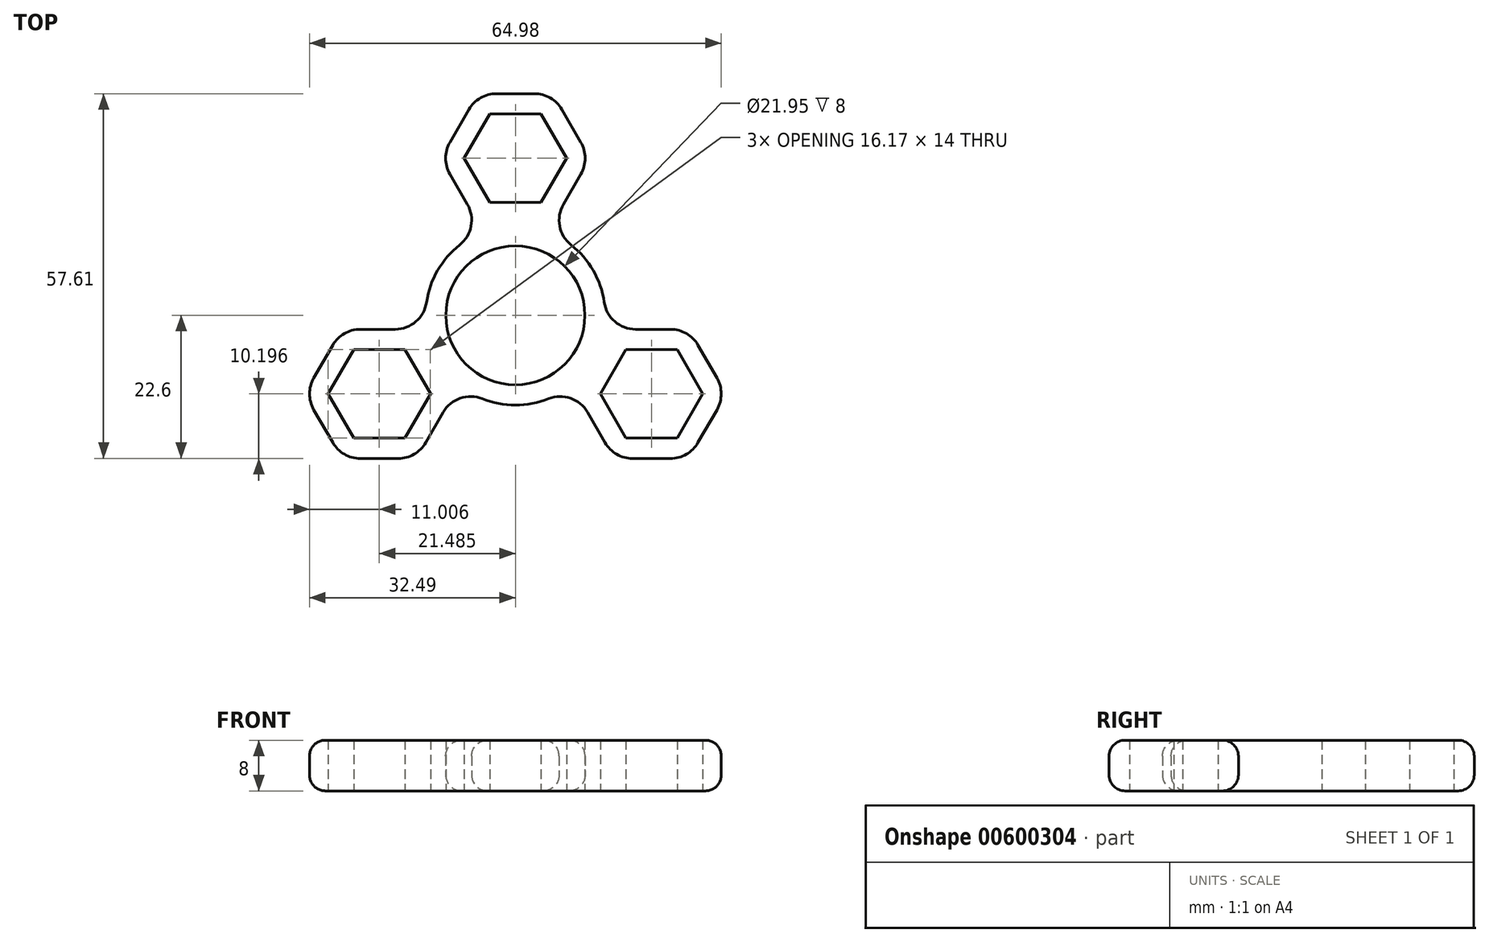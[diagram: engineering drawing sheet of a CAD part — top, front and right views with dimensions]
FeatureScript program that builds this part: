
annotation { "Feature Type Name" : "Feature", "Feature Type Description" : "" }
export const myFeature = defineFeature(function(context is Context, id is Id, definition is map)
    precondition{}
    {
        {
            var Q0;
            Q0=qCreatedBy(makeId("Top.planeOp"),FACE);
            var sketch = newSketch(context, id + "F0", { "sketchPlane" : qUnion([Q0])});
            skCircle(sketch, "E0", {"center": v(0, 0) * mm, "radius": 35.5 * mm, "construction": true});
            skLineSegment(sketch, "E1", {"start": v(0, 24.8) * mm, "end": v(0, 0) * mm, "construction": true});
            skLineSegment(sketch, "E2", {"start": v(0, 0) * mm, "end": v(-21.48, -12.4) * mm, "construction": true});
            skLineSegment(sketch, "E3", {"start": v(0, 0) * mm, "end": v(21.48, -12.4) * mm, "construction": true});
            skCircle(sketch, "E4.cCircle", {"center": v(0, 24.8) * mm, "radius": 7 * mm, "construction": true});
            skLineSegment(sketch, "E4.0", {"start": v(8.08, 24.8) * mm, "end": v(4.04, 17.8) * mm});
            skLineSegment(sketch, "E4.1", {"start": v(4.04, 17.8) * mm, "end": v(-4.04, 17.8) * mm});
            skLineSegment(sketch, "E4.2", {"start": v(-4.04, 17.8) * mm, "end": v(-8.08, 24.8) * mm});
            skLineSegment(sketch, "E4.3", {"start": v(-8.08, 24.8) * mm, "end": v(-4.04, 31.8) * mm});
            skLineSegment(sketch, "E4.4", {"start": v(-4.04, 31.8) * mm, "end": v(4.04, 31.8) * mm});
            skLineSegment(sketch, "E4.5", {"start": v(4.04, 31.8) * mm, "end": v(8.08, 24.8) * mm});
            skPoint(sketch, "E4.0.midPoint", {"position": v(6.06, 21.3) * mm});
            skCircle(sketch, "E5.cCircle", {"center": v(0, 24.8) * mm, "radius": 10.2 * mm, "construction": true});
            skLineSegment(sketch, "E5.0", {"start": v(11.78, 24.8) * mm, "end": v(5.89, 14.6) * mm});
            skLineSegment(sketch, "E5.1", {"start": v(5.89, 14.6) * mm, "end": v(-5.89, 14.6) * mm});
            skLineSegment(sketch, "E5.2", {"start": v(-5.89, 14.6) * mm, "end": v(-11.78, 24.8) * mm});
            skLineSegment(sketch, "E5.3", {"start": v(-11.78, 24.8) * mm, "end": v(-5.89, 35) * mm});
            skLineSegment(sketch, "E5.4", {"start": v(-5.89, 35) * mm, "end": v(5.89, 35) * mm});
            skLineSegment(sketch, "E5.5", {"start": v(5.89, 35) * mm, "end": v(11.78, 24.8) * mm});
            skPoint(sketch, "E5.0.midPoint", {"position": v(8.83, 19.7) * mm});
            skLineSegment(sketch, "E6", {"start": v(-5.89, 14.6) * mm, "end": v(-5.1, 13.23) * mm});
            skLineSegment(sketch, "E7", {"start": v(5.89, 14.6) * mm, "end": v(5.1, 13.23) * mm});
            skCircle(sketch, "E8", {"center": v(0, 0) * mm, "radius": 10.97 * mm});
            skCircle(sketch, "E9.cCircle", {"center": v(21.48, -12.4) * mm, "radius": 7 * mm, "construction": true});
            skLineSegment(sketch, "E9.0", {"start": v(29.57, -12.4) * mm, "end": v(25.53, -19.4) * mm});
            skLineSegment(sketch, "E9.1", {"start": v(25.53, -19.4) * mm, "end": v(17.44, -19.4) * mm});
            skLineSegment(sketch, "E9.2", {"start": v(17.44, -19.4) * mm, "end": v(13.4, -12.4) * mm});
            skLineSegment(sketch, "E9.3", {"start": v(13.4, -12.4) * mm, "end": v(17.44, -5.4) * mm});
            skLineSegment(sketch, "E9.4", {"start": v(17.44, -5.4) * mm, "end": v(25.53, -5.4) * mm});
            skLineSegment(sketch, "E9.5", {"start": v(25.53, -5.4) * mm, "end": v(29.57, -12.4) * mm});
            skPoint(sketch, "E9.0.midPoint", {"position": v(27.55, -15.9) * mm});
            skCircle(sketch, "E10.cCircle", {"center": v(21.48, -12.4) * mm, "radius": 10.2 * mm, "construction": true});
            skLineSegment(sketch, "E10.0", {"start": v(33.26, -12.4) * mm, "end": v(27.37, -22.6) * mm});
            skLineSegment(sketch, "E10.1", {"start": v(27.37, -22.6) * mm, "end": v(15.6, -22.6) * mm});
            skLineSegment(sketch, "E10.2", {"start": v(15.6, -22.6) * mm, "end": v(9.7, -12.4) * mm});
            skLineSegment(sketch, "E10.3", {"start": v(9.7, -12.4) * mm, "end": v(15.6, -2.2) * mm});
            skLineSegment(sketch, "E10.4", {"start": v(15.6, -2.2) * mm, "end": v(27.37, -2.2) * mm});
            skLineSegment(sketch, "E10.5", {"start": v(27.37, -2.2) * mm, "end": v(33.26, -12.4) * mm});
            skPoint(sketch, "E10.0.midPoint", {"position": v(30.32, -17.5) * mm});
            skCircle(sketch, "E11.cCircle", {"center": v(-21.48, -12.4) * mm, "radius": 7 * mm, "construction": true});
            skLineSegment(sketch, "E11.0", {"start": v(-13.4, -12.4) * mm, "end": v(-17.44, -19.4) * mm});
            skLineSegment(sketch, "E11.1", {"start": v(-17.44, -19.4) * mm, "end": v(-25.53, -19.4) * mm});
            skLineSegment(sketch, "E11.2", {"start": v(-25.53, -19.4) * mm, "end": v(-29.57, -12.4) * mm});
            skLineSegment(sketch, "E11.3", {"start": v(-29.57, -12.4) * mm, "end": v(-25.53, -5.4) * mm});
            skLineSegment(sketch, "E11.4", {"start": v(-25.53, -5.4) * mm, "end": v(-17.44, -5.4) * mm});
            skLineSegment(sketch, "E11.5", {"start": v(-17.44, -5.4) * mm, "end": v(-13.4, -12.4) * mm});
            skPoint(sketch, "E11.0.midPoint", {"position": v(-15.42, -15.9) * mm});
            skCircle(sketch, "E12.cCircle", {"center": v(-21.48, -12.4) * mm, "radius": 10.2 * mm, "construction": true});
            skLineSegment(sketch, "E12.0", {"start": v(-9.7, -12.4) * mm, "end": v(-15.6, -22.6) * mm});
            skLineSegment(sketch, "E12.1", {"start": v(-15.6, -22.6) * mm, "end": v(-27.37, -22.6) * mm});
            skLineSegment(sketch, "E12.2", {"start": v(-27.37, -22.6) * mm, "end": v(-33.26, -12.4) * mm});
            skLineSegment(sketch, "E12.3", {"start": v(-33.26, -12.4) * mm, "end": v(-27.37, -2.2) * mm});
            skLineSegment(sketch, "E12.4", {"start": v(-27.37, -2.2) * mm, "end": v(-15.6, -2.2) * mm});
            skLineSegment(sketch, "E12.5", {"start": v(-15.6, -2.2) * mm, "end": v(-9.7, -12.4) * mm});
            skPoint(sketch, "E12.0.midPoint", {"position": v(-12.65, -17.5) * mm});
            skLineSegment(sketch, "E13", {"start": v(-15.6, -2.2) * mm, "end": v(-14, -2.2) * mm});
            skLineSegment(sketch, "E14", {"start": v(-9.7, -12.4) * mm, "end": v(-8.91, -11.02) * mm});
            skLineSegment(sketch, "E15", {"start": v(9.7, -12.4) * mm, "end": v(8.91, -11.02) * mm});
            skLineSegment(sketch, "E16", {"start": v(15.6, -2.2) * mm, "end": v(14, -2.2) * mm});
            skCircle(sketch, "E17", {"center": v(0, 0) * mm, "radius": 14.18 * mm});
            skSolve(sketch);
        }
        {
            var Q0;
            Q0=qSketchRegion(id+"F0",true);
            extrude(context, id + "F1", {"entities" : qUnion([Q0]), "endBound" : BoundingType.SYMMETRIC, "depth" : 8 * mm, "offsetDistance" : 25 * mm});
        }
        {
            var Q0;
            Q0=makeQuery(id+"F1.opExtrude","SWEPT_EDGE",EDGE,{"disambiguationData":[OSD([sQuery(id+"F0.wireOp",EDGE,"O4FCEVp2-a76e-EbQX-IVHh-MGuyo65jWMq8"),sQuery(id+"F0.wireOp",EDGE,"E6")])]});
            var Q1;
            Q1=makeQuery(id+"F1.opExtrude","SWEPT_EDGE",EDGE,{"disambiguationData":[OSD([sQuery(id+"F0.wireOp",EDGE,"O4FCEVp2-a76e-EbQX-IVHh-MGuyo65jWMq8"),sQuery(id+"F0.wireOp",EDGE,"E13")])]});
            var Q2;
            Q2=makeQuery(id+"F1.opExtrude","SWEPT_EDGE",EDGE,{"disambiguationData":[OSD([sQuery(id+"F0.wireOp",EDGE,"O4FCEVp2-a76e-EbQX-IVHh-MGuyo65jWMq8"),sQuery(id+"F0.wireOp",EDGE,"E15")])]});
            var Q3;
            Q3=makeQuery(id+"F1.opExtrude","SWEPT_EDGE",EDGE,{"disambiguationData":[OSD([sQuery(id+"F0.wireOp",EDGE,"O4FCEVp2-a76e-EbQX-IVHh-MGuyo65jWMq8"),sQuery(id+"F0.wireOp",EDGE,"E14")])]});
            var Q4;
            Q4=makeQuery(id+"F1.opExtrude","SWEPT_EDGE",EDGE,{"disambiguationData":[OSD([sQuery(id+"F0.wireOp",EDGE,"O4FCEVp2-a76e-EbQX-IVHh-MGuyo65jWMq8"),sQuery(id+"F0.wireOp",EDGE,"E16")])]});
            var Q5;
            Q5=makeQuery(id+"F1.opExtrude","SWEPT_EDGE",EDGE,{"disambiguationData":[OSD([sQuery(id+"F0.wireOp",EDGE,"O4FCEVp2-a76e-EbQX-IVHh-MGuyo65jWMq8"),sQuery(id+"F0.wireOp",EDGE,"E7")])]});
            var Q6;
            Q6=makeQuery(id+"F1.opExtrude","SWEPT_EDGE",EDGE,{"disambiguationData":[OSD([sQuery(id+"F0.wireOp",EDGE,"E10.4"),sQuery(id+"F0.wireOp",EDGE,"E10.5")])]});
            var Q7;
            Q7=makeQuery(id+"F1.opExtrude","SWEPT_EDGE",EDGE,{"disambiguationData":[OSD([sQuery(id+"F0.wireOp",EDGE,"E10.0"),sQuery(id+"F0.wireOp",EDGE,"E10.5")])]});
            var Q8;
            Q8=makeQuery(id+"F1.opExtrude","SWEPT_EDGE",EDGE,{"disambiguationData":[OSD([sQuery(id+"F0.wireOp",EDGE,"E10.0"),sQuery(id+"F0.wireOp",EDGE,"E10.1")])]});
            var Q9;
            Q9=makeQuery(id+"F1.opExtrude","SWEPT_EDGE",EDGE,{"disambiguationData":[OSD([sQuery(id+"F0.wireOp",EDGE,"E10.1"),sQuery(id+"F0.wireOp",EDGE,"E10.2")])]});
            var Q10;
            Q10=makeQuery(id+"F1.opExtrude","SWEPT_EDGE",EDGE,{"disambiguationData":[OSD([sQuery(id+"F0.wireOp",EDGE,"E12.0"),sQuery(id+"F0.wireOp",EDGE,"E12.1")])]});
            var Q11;
            Q11=makeQuery(id+"F1.opExtrude","SWEPT_EDGE",EDGE,{"disambiguationData":[OSD([sQuery(id+"F0.wireOp",EDGE,"E12.1"),sQuery(id+"F0.wireOp",EDGE,"E12.2")])]});
            var Q12;
            Q12=makeQuery(id+"F1.opExtrude","SWEPT_EDGE",EDGE,{"disambiguationData":[OSD([sQuery(id+"F0.wireOp",EDGE,"E12.2"),sQuery(id+"F0.wireOp",EDGE,"E12.3")])]});
            var Q13;
            Q13=makeQuery(id+"F1.opExtrude","SWEPT_EDGE",EDGE,{"disambiguationData":[OSD([sQuery(id+"F0.wireOp",EDGE,"E12.3"),sQuery(id+"F0.wireOp",EDGE,"E12.4")])]});
            var Q14;
            Q14=makeQuery(id+"F1.opExtrude","SWEPT_EDGE",EDGE,{"disambiguationData":[OSD([sQuery(id+"F0.wireOp",EDGE,"E5.2"),sQuery(id+"F0.wireOp",EDGE,"E5.3")])]});
            var Q15;
            Q15=makeQuery(id+"F1.opExtrude","SWEPT_EDGE",EDGE,{"disambiguationData":[OSD([sQuery(id+"F0.wireOp",EDGE,"E5.3"),sQuery(id+"F0.wireOp",EDGE,"E5.4")])]});
            var Q16;
            Q16=makeQuery(id+"F1.opExtrude","SWEPT_EDGE",EDGE,{"disambiguationData":[OSD([sQuery(id+"F0.wireOp",EDGE,"E5.4"),sQuery(id+"F0.wireOp",EDGE,"E5.5")])]});
            var Q17;
            Q17=makeQuery(id+"F1.opExtrude","SWEPT_EDGE",EDGE,{"disambiguationData":[OSD([sQuery(id+"F0.wireOp",EDGE,"E5.0"),sQuery(id+"F0.wireOp",EDGE,"E5.5")])]});
            fillet(context, id + "F2", {"entities" : qUnion([Q0, Q1, Q2, Q3, Q4, Q5, Q6, Q7, Q8, Q9, Q10, Q11, Q12, Q13, Q14, Q15, Q16, Q17]), "radius" : 5 * mm, "tangentPropagation" : true, "allowEdgeOverflow" : false});
        }
        {
            var Q0;
            Q0=makeQuery(id+"F1.opExtrude","SWEPT_FACE",FACE,{"disambiguationData":[OSD([sQuery(id+"F0.wireOp",EDGE,"E5.3"),sQuery(id+"F0.wireOp",EDGE,"E12.3"),sQuery(id+"F0.wireOp",EDGE,"RTg8jkj1-B7h5-RVuZ-TKbk-OqO4RIGME4TE")])]});
            fillet(context, id + "F3", {"entities" : qUnion([Q0]), "radius" : 2.5 * mm, "tangentPropagation" : true, "allowEdgeOverflow" : false});
        }
    });
